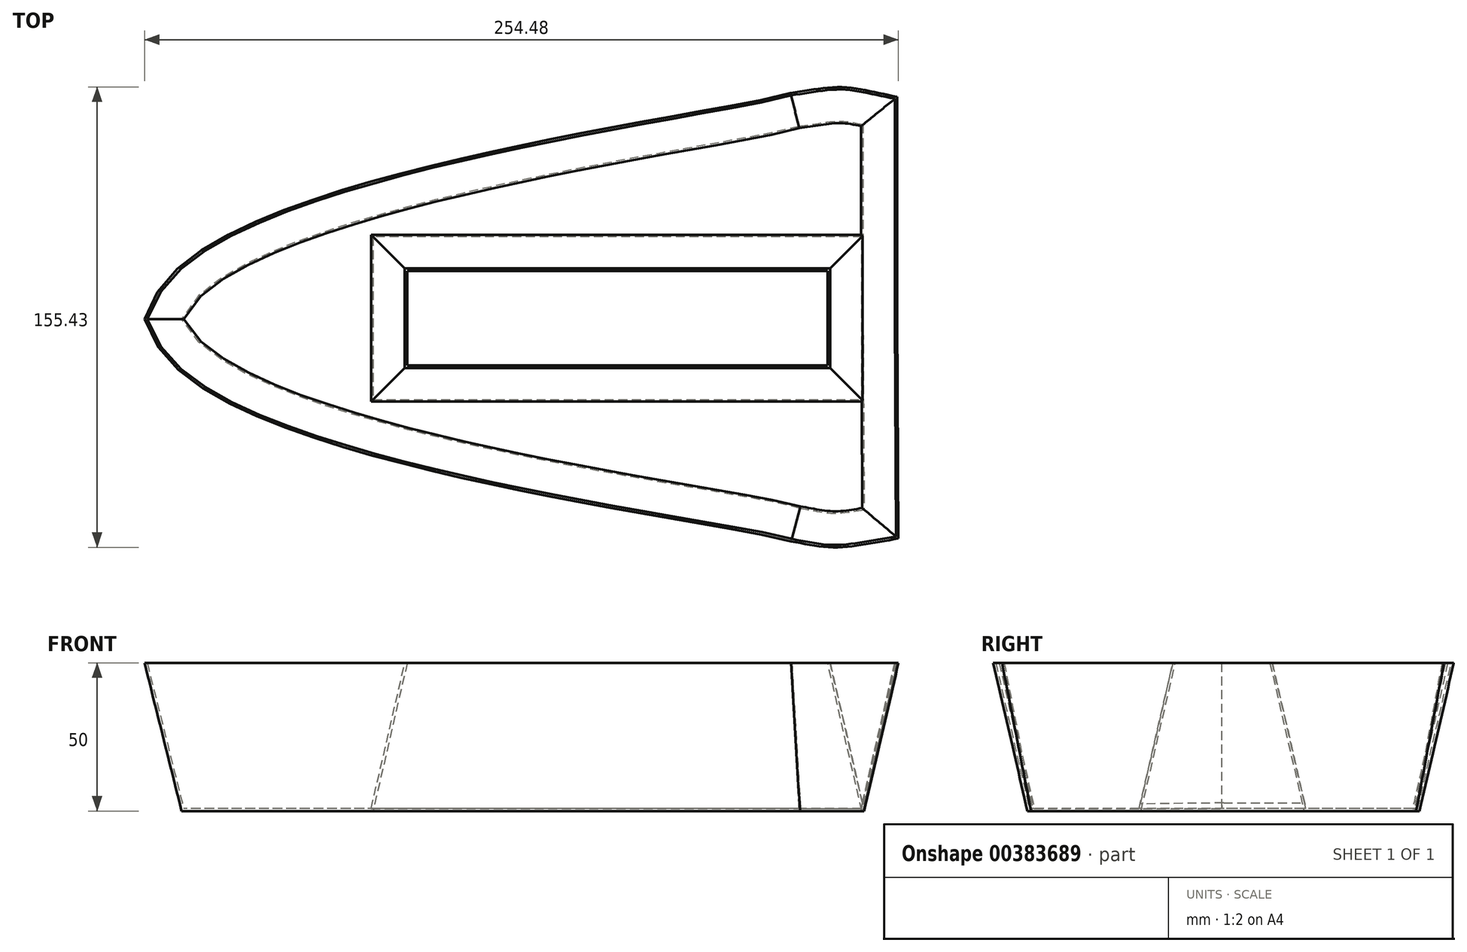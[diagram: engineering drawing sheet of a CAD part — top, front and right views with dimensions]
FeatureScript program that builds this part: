
annotation { "Feature Type Name" : "Feature", "Feature Type Description" : "" }
export const myFeature = defineFeature(function(context is Context, id is Id, definition is map)
    precondition{}
    {
        {
            var Q0;
            Q0=qCreatedBy(makeId("Top.planeOp"),FACE);
            var sketch = newSketch(context, id + "F0", { "sketchPlane" : qUnion([Q0])});
            skFitSpline(sketch, "E0", {"points": [v(94.58, 64.6) * mm, v(-113.76, -0.48) * mm], "startDerivative": vector(-50.54, -18.05) * mm, "endDerivative": vector(-47.72, -114.02) * mm});
            skLineSegment(sketch, "E1", {"start": v(116.24, 0.2) * mm, "end": v(116.24, 65.2) * mm});
            skLineSegment(sketch, "E2", {"start": v(116.24, 0.2) * mm, "end": v(-128.28, -0.48) * mm});
            skFitSpline(sketch, "E3.MirrorCS", {"points": [v(94.94, -64.32) * mm, v(-113.76, -0.4) * mm], "startDerivative": vector(-50.64, 17.77) * mm, "endDerivative": vector(-48.36, 113.75) * mm});
            skLineSegment(sketch, "E4.MirrorCS", {"start": v(116.24, 0.2) * mm, "end": v(116.6, -64.8) * mm});
            skFitSpline(sketch, "E5", {"points": [v(94.58, 64.6) * mm, v(116.24, 65.2) * mm], "startDerivative": vector(40.13, 6.16) * mm, "endDerivative": vector(24.84, -5.24) * mm});
            skFitSpline(sketch, "E6", {"points": [v(94.94, -64.32) * mm, v(116.6, -64.8) * mm], "startDerivative": vector(34.64, -6.5) * mm, "endDerivative": vector(30.35, 5.05) * mm});
            skLineSegment(sketch, "E7.bottom", {"start": v(-49.15, -27.66) * mm, "end": v(115.85, -27.66) * mm});
            skLineSegment(sketch, "E7.top", {"start": v(-49.15, 27.34) * mm, "end": v(115.85, 27.34) * mm});
            skLineSegment(sketch, "E7.left", {"start": v(-49.15, -27.66) * mm, "end": v(-49.15, 27.34) * mm});
            skLineSegment(sketch, "E7.right", {"start": v(115.85, -27.66) * mm, "end": v(115.85, 27.34) * mm});
            skSolve(sketch);
        }
        {
            var Q0;
            {var subQ0=sQuery(id+"F0.wireOp",EDGE,"E4.MirrorCS");Q0=makeQuery(id+"F0.imprint","IMPRINT",FACE,{"disambiguationData":[TD([[makeQuery(id+"F0.imprint","IMPRINT",EDGE,{"derivedFrom":subQ0}),-1.0]])]});}
            var Q1;
            {var subQ4=sQuery(id+"F0.wireOp",EDGE,"E1");Q1=makeQuery(id+"F0.imprint","IMPRINT",FACE,{"disambiguationData":[TD([[makeQuery(id+"F0.imprint","IMPRINT",EDGE,{"derivedFrom":subQ4}),1.0]])]});}
            extrude(context, id + "F1", {"entities" : qUnion([Q0, Q1]), "depth" : 50 * mm, "hasDraft" : true, "draftAngle" : 13 * degree});
        }
        {
            var Q0;
            Q0=makeQuery(id+"F1.opExtrude","CAP_FACE",FACE,{"disambiguationData":[OSD([sQuery(id+"F0.wireOp",EDGE,"E0"),sQuery(id+"F0.wireOp",EDGE,"E1"),sQuery(id+"F0.wireOp",EDGE,"E3.MirrorCS"),sQuery(id+"F0.wireOp",EDGE,"E4.MirrorCS"),sQuery(id+"F0.wireOp",EDGE,"E5"),sQuery(id+"F0.wireOp",EDGE,"E6")])],"isStart":false});
            shell(context, id + "F2", {"entities" : qUnion([Q0]), "thickness" : 0.8 * mm});
        }
    });
